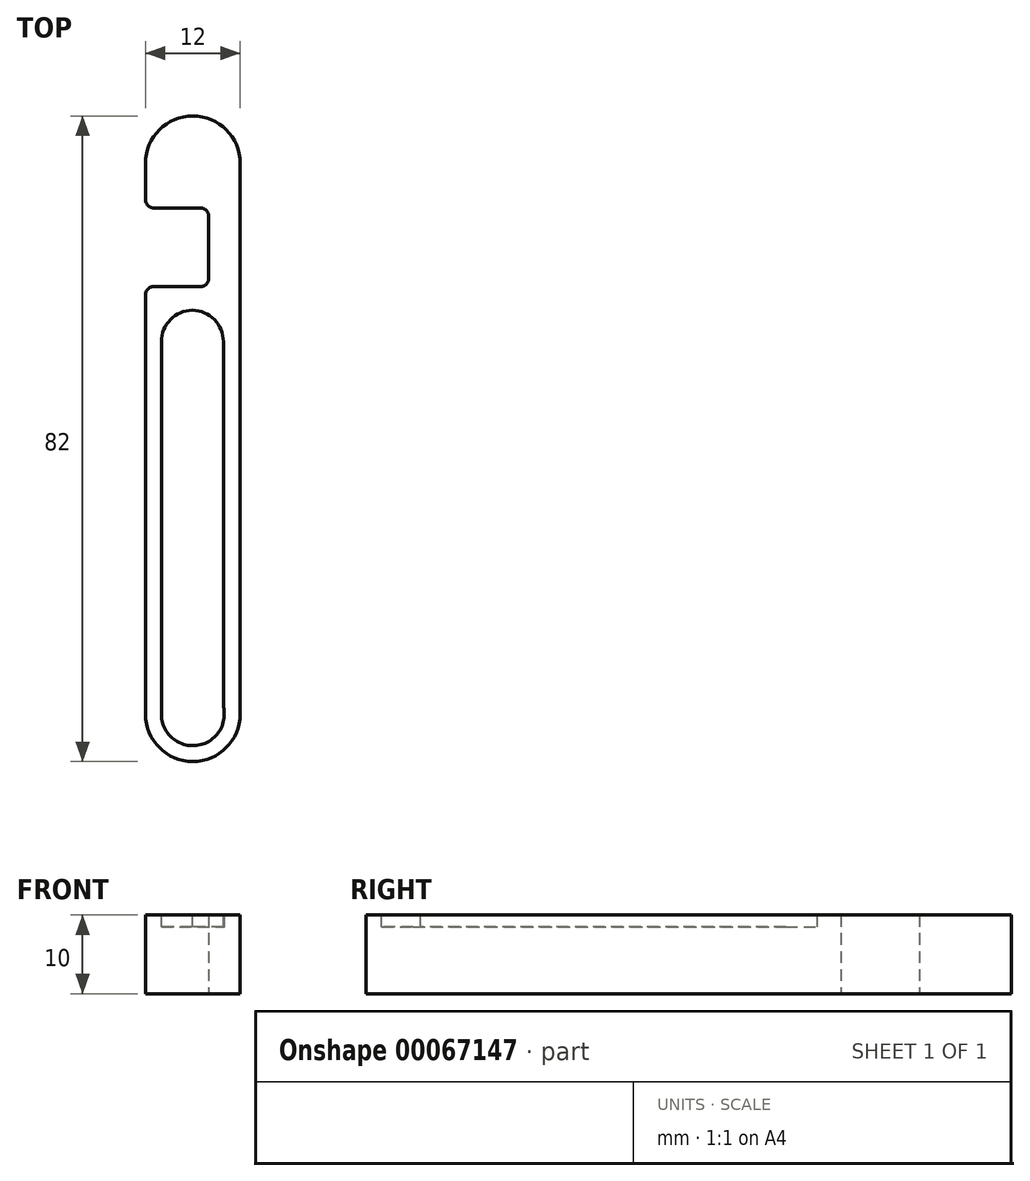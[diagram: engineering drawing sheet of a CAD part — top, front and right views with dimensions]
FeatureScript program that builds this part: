
annotation { "Feature Type Name" : "Feature", "Feature Type Description" : "" }
export const myFeature = defineFeature(function(context is Context, id is Id, definition is map)
    precondition{}
    {
        {
            var Q0;
            Q0=qCreatedBy(makeId("Top.planeOp"),FACE);
            var sketch = newSketch(context, id + "F0", { "sketchPlane" : qUnion([Q0])});
            skLineSegment(sketch, "E0.rect.bottom", {"start": v(0, 41) * mm, "end": v(0, 41) * mm});
            skLineSegment(sketch, "E0.rect.top", {"start": v(0, -41) * mm, "end": v(0, -41) * mm});
            skLineSegment(sketch, "E0.rect.left", {"start": v(-6, 18.32) * mm, "end": v(-6, -35) * mm});
            skLineSegment(sketch, "E0.rect.right", {"start": v(6, 35) * mm, "end": v(6, -35) * mm});
            skPoint(sketch, "E0.rect.middle", {"position": v(0, 0) * mm});
            skPoint(sketch, "E1.visualSharp", {"position": v(-6, 41) * mm});
            skArc(sketch, "E1.filletArc", {"start": v(0, 41) * mm, "mid": v(-4.24, 39.24) * mm, "end": v(-6, 35) * mm});
            skPoint(sketch, "E2.visualSharp", {"position": v(6, 41) * mm});
            skArc(sketch, "E2.filletArc", {"start": v(6, 35) * mm, "mid": v(4.24, 39.24) * mm, "end": v(0, 41) * mm});
            skPoint(sketch, "E3.visualSharp", {"position": v(6, -41) * mm});
            skArc(sketch, "E3.filletArc", {"start": v(0, -41) * mm, "mid": v(4.24, -39.24) * mm, "end": v(6, -35) * mm});
            skPoint(sketch, "E4.visualSharp", {"position": v(-6, -41) * mm});
            skArc(sketch, "E4.filletArc", {"start": v(-6, -35) * mm, "mid": v(-4.24, -39.24) * mm, "end": v(0, -41) * mm});
            skLineSegment(sketch, "E5", {"start": v(-6, 30.32) * mm, "end": v(-6, 35) * mm});
            skLineSegment(sketch, "E6", {"start": v(-5, 29.32) * mm, "end": v(1, 29.32) * mm});
            skLineSegment(sketch, "E7", {"start": v(2, 28.32) * mm, "end": v(2, 20.32) * mm});
            skPoint(sketch, "E7.endSnap0", {"position": v(2, 29.32) * mm});
            skLineSegment(sketch, "E8", {"start": v(1, 19.32) * mm, "end": v(-5, 19.32) * mm});
            skPoint(sketch, "E9.visualSharp", {"position": v(-6, 29.32) * mm});
            skArc(sketch, "E9.filletArc", {"start": v(-6, 30.32) * mm, "mid": v(-5.7, 29.61) * mm, "end": v(-5, 29.32) * mm});
            skPoint(sketch, "E10.visualSharp", {"position": v(-6, 19.32) * mm});
            skArc(sketch, "E10.filletArc", {"start": v(-5, 19.32) * mm, "mid": v(-5.7, 19.03) * mm, "end": v(-6, 18.32) * mm});
            skArc(sketch, "E11.filletArc", {"start": v(2, 28.32) * mm, "mid": v(1.7, 29.03) * mm, "end": v(1, 29.32) * mm});
            skPoint(sketch, "E12.visualSharp", {"position": v(2, 19.32) * mm});
            skArc(sketch, "E12.filletArc", {"start": v(1, 19.32) * mm, "mid": v(1.7, 19.61) * mm, "end": v(2, 20.32) * mm});
            skSolve(sketch);
        }
        {
            var Q0;
            Q0 = qSketchRegion(id + "F0", true);
            extrude(context, id + "F1", {"entities" : qUnion([Q0]), "endBound" : BoundingType.SYMMETRIC, "depth" : 10 * mm});
        }
        {
            var Q0;
            Q0=makeQuery(id+"F1.opExtrude","CAP_FACE",FACE,{"disambiguationData":[OSD([sQuery(id+"F0.wireOp",EDGE,"E0.rect.left"),sQuery(id+"F0.wireOp",EDGE,"E0.rect.right"),sQuery(id+"F0.wireOp",EDGE,"E1.filletArc"),sQuery(id+"F0.wireOp",EDGE,"E2.filletArc"),sQuery(id+"F0.wireOp",EDGE,"E3.filletArc"),sQuery(id+"F0.wireOp",EDGE,"E4.filletArc"),sQuery(id+"F0.wireOp",EDGE,"E5"),sQuery(id+"F0.wireOp",EDGE,"E6"),sQuery(id+"F0.wireOp",EDGE,"E7"),sQuery(id+"F0.wireOp",EDGE,"E8"),sQuery(id+"F0.wireOp",EDGE,"E9.filletArc"),sQuery(id+"F0.wireOp",EDGE,"E10.filletArc"),sQuery(id+"F0.wireOp",EDGE,"E11.filletArc"),sQuery(id+"F0.wireOp",EDGE,"E12.filletArc")])],"isStart":false});
            var sketch = newSketch(context, id + "F2", { "sketchPlane" : qUnion([Q0])});
            skArc(sketch, "E13.0", {"start": v(-4, -35) * mm, "mid": v(-2.83, -37.83) * mm, "end": v(0, -39) * mm});
            skArc(sketch, "E14.0", {"start": v(0, -39) * mm, "mid": v(3.15, -37.47) * mm, "end": v(3.89, -34.05) * mm});
            skLineSegment(sketch, "E15", {"start": v(-4, -35) * mm, "end": v(-4, 12.32) * mm});
            skLineSegment(sketch, "E16", {"start": v(-0.11, 16.32) * mm, "end": v(0, 16.32) * mm});
            skLineSegment(sketch, "E17", {"start": v(3.89, 12.32) * mm, "end": v(3.89, -34.05) * mm});
            skPoint(sketch, "E18.visualSharp", {"position": v(3.89, 16.32) * mm});
            skArc(sketch, "E18.filletArc", {"start": v(3.89, 12.32) * mm, "mid": v(2.71, 15.15) * mm, "end": v(-0.11, 16.32) * mm});
            skPoint(sketch, "E19.visualSharp", {"position": v(-4, 16.32) * mm});
            skArc(sketch, "E19.filletArc", {"start": v(0, 16.32) * mm, "mid": v(-2.83, 15.15) * mm, "end": v(-4, 12.32) * mm});
            skSolve(sketch);
        }
        {
            var Q0;
            Q0=makeQuery(id+"F2.imprint","IMPRINT",FACE,{"disambiguationData":[TD([[makeQuery(id+"F2.imprint","IMPRINT",EDGE,{"derivedFrom":sQuery(id+"F2.wireOp",EDGE,"E13.0")}),1.0]])]});
            extrude(context, id + "F3", {"entities" : qUnion([Q0]), "operationType" : NewBodyOperationType.REMOVE, "endBound" : BoundingType.SYMMETRIC, "oppositeDirection" : true, "depth" : 3 * mm});
        }
    });
